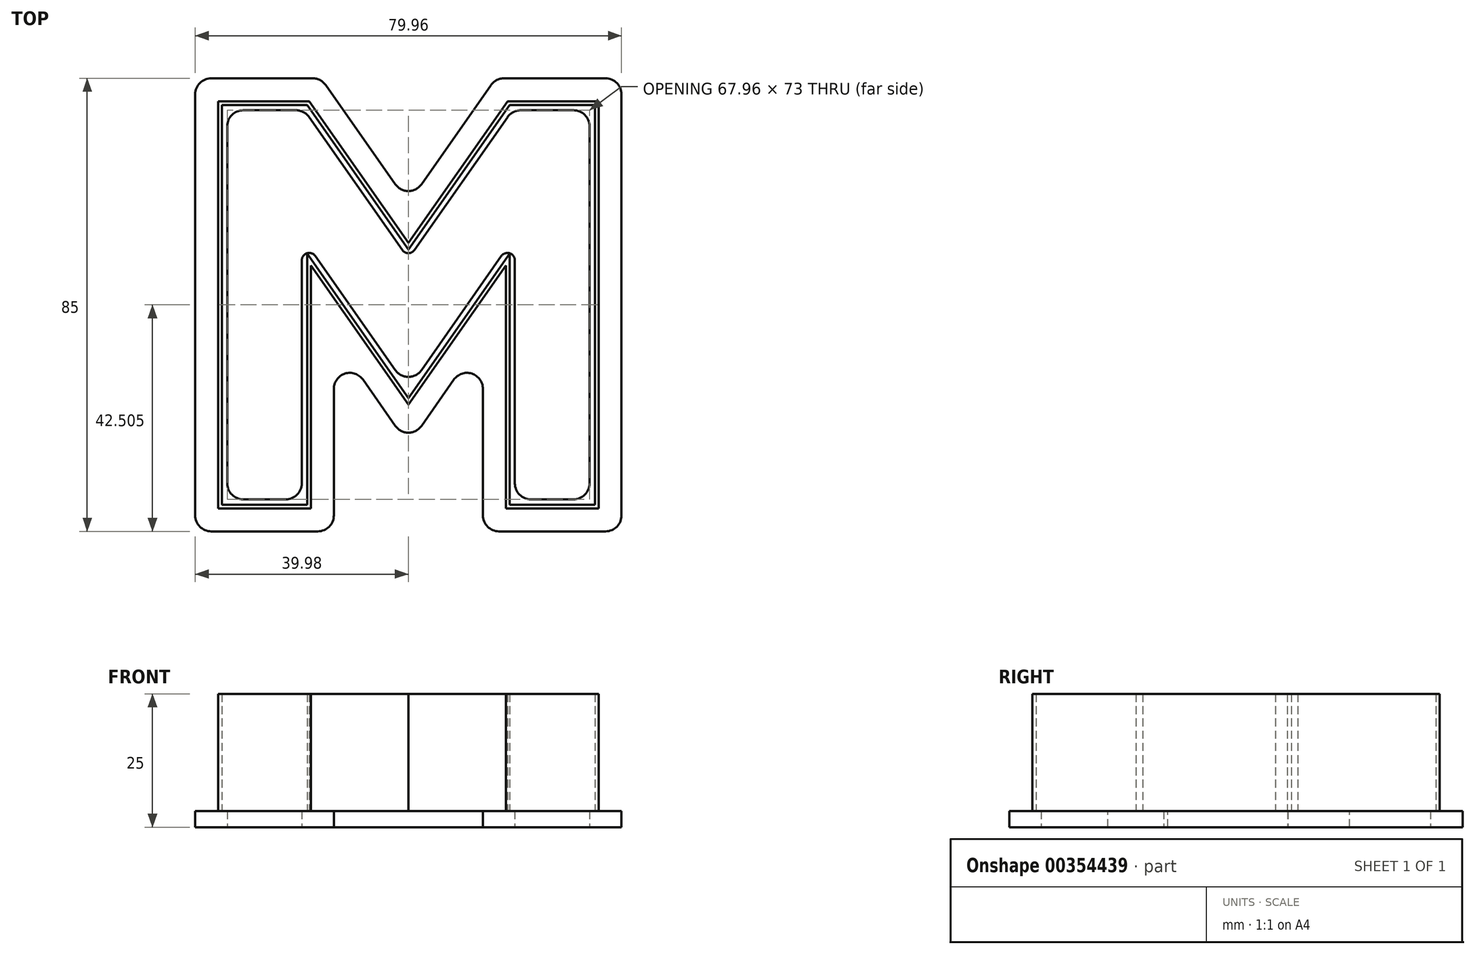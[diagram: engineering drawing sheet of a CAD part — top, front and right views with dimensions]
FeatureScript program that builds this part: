
annotation { "Feature Type Name" : "Feature", "Feature Type Description" : "" }
export const myFeature = defineFeature(function(context is Context, id is Id, definition is map)
    precondition{}
    {
        {
            var Q0;
            Q0=qCreatedBy(makeId("Top.planeOp"),FACE);
            var sketch = newSketch(context, id + "F0", { "sketchPlane" : qUnion([Q0])});
            skLineSegment(sketch, "E0", {"start": v(-34.98, -47.9) * mm, "end": v(-34.98, 27.1) * mm});
            skLineSegment(sketch, "E1", {"start": v(-34.98, 27.1) * mm, "end": v(-18.98, 27.1) * mm});
            skLineSegment(sketch, "E2", {"start": v(-18.98, 27.1) * mm, "end": v(0, 0) * mm});
            skLineSegment(sketch, "E3", {"start": v(0, 0) * mm, "end": v(18.98, 27.1) * mm});
            skLineSegment(sketch, "E4", {"start": v(18.98, 27.1) * mm, "end": v(34.98, 27.1) * mm});
            skLineSegment(sketch, "E5", {"start": v(34.98, 27.1) * mm, "end": v(34.98, -47.9) * mm});
            skLineSegment(sketch, "E6", {"start": v(34.98, -47.9) * mm, "end": v(18.98, -47.9) * mm});
            skLineSegment(sketch, "E7", {"start": v(18.98, -47.9) * mm, "end": v(18.98, -0.8) * mm});
            skLineSegment(sketch, "E8", {"start": v(18.98, -0.8) * mm, "end": v(0, -27.9) * mm});
            skLineSegment(sketch, "E9", {"start": v(-34.98, -47.9) * mm, "end": v(-18.98, -47.9) * mm});
            skLineSegment(sketch, "E10", {"start": v(-18.98, -47.9) * mm, "end": v(-18.98, -0.8) * mm});
            skLineSegment(sketch, "E11", {"start": v(-18.98, -0.8) * mm, "end": v(0, -27.9) * mm});
            skLineSegment(sketch, "E12", {"start": v(0, 0) * mm, "end": v(0, -47.9) * mm, "construction": true});
            skLineSegment(sketch, "E13", {"start": v(-18.98, -47.9) * mm, "end": v(0, -47.9) * mm, "construction": true});
            skLineSegment(sketch, "E14", {"start": v(0, -47.9) * mm, "end": v(18.98, -47.9) * mm, "construction": true});
            skLineSegment(sketch, "E15", {"start": v(-18.98, 27.1) * mm, "end": v(18.98, 27.1) * mm, "construction": true});
            skLineSegment(sketch, "E16.0", {"start": v(-33.98, -46.9) * mm, "end": v(-33.98, 26.1) * mm});
            skLineSegment(sketch, "E16.1", {"start": v(33.98, 26.1) * mm, "end": v(33.98, -46.9) * mm});
            skLineSegment(sketch, "E16.2", {"start": v(19.5, 26.1) * mm, "end": v(33.98, 26.1) * mm});
            skLineSegment(sketch, "E16.3", {"start": v(0, -1.74) * mm, "end": v(19.5, 26.1) * mm});
            skLineSegment(sketch, "E16.4", {"start": v(-19.5, 26.1) * mm, "end": v(0, -1.74) * mm});
            skLineSegment(sketch, "E16.5", {"start": v(33.98, -46.9) * mm, "end": v(19.98, -46.9) * mm});
            skLineSegment(sketch, "E16.6", {"start": v(-33.98, 26.1) * mm, "end": v(-19.5, 26.1) * mm});
            skLineSegment(sketch, "E16.7", {"start": v(19.98, -46.9) * mm, "end": v(19.98, 2.38) * mm});
            skLineSegment(sketch, "E16.8", {"start": v(19.98, 2.38) * mm, "end": v(0, -26.15) * mm});
            skLineSegment(sketch, "E16.9", {"start": v(-19.98, 2.38) * mm, "end": v(0, -26.15) * mm});
            skLineSegment(sketch, "E16.10", {"start": v(-19.98, -46.9) * mm, "end": v(-19.98, 2.38) * mm});
            skLineSegment(sketch, "E16.11", {"start": v(-33.98, -46.9) * mm, "end": v(-19.98, -46.9) * mm});
            skLineSegment(sketch, "E17.0", {"start": v(-39.98, -52.9) * mm, "end": v(-13.98, -52.9) * mm});
            skLineSegment(sketch, "E17.1", {"start": v(16.38, 32.1) * mm, "end": v(39.98, 32.1) * mm});
            skLineSegment(sketch, "E17.2", {"start": v(0, 8.72) * mm, "end": v(16.38, 32.1) * mm});
            skLineSegment(sketch, "E17.3", {"start": v(-16.38, 32.1) * mm, "end": v(0, 8.72) * mm});
            skLineSegment(sketch, "E17.4", {"start": v(-39.98, 32.1) * mm, "end": v(-16.38, 32.1) * mm});
            skLineSegment(sketch, "E17.5", {"start": v(39.98, 32.1) * mm, "end": v(39.98, -52.9) * mm});
            skLineSegment(sketch, "E17.6", {"start": v(-39.98, -52.9) * mm, "end": v(-39.98, 32.1) * mm});
            skLineSegment(sketch, "E17.7", {"start": v(39.98, -52.9) * mm, "end": v(13.98, -52.9) * mm});
            skLineSegment(sketch, "E17.8", {"start": v(13.98, -52.9) * mm, "end": v(13.98, -16.65) * mm});
            skLineSegment(sketch, "E17.9", {"start": v(13.98, -16.65) * mm, "end": v(0, -36.61) * mm});
            skLineSegment(sketch, "E17.10", {"start": v(-13.98, -16.65) * mm, "end": v(0, -36.61) * mm});
            skLineSegment(sketch, "E17.11", {"start": v(-13.98, -52.9) * mm, "end": v(-13.98, -16.65) * mm});
            skLineSegment(sketch, "E18.0", {"start": v(-35.68, -48.6) * mm, "end": v(-18.28, -48.6) * mm});
            skLineSegment(sketch, "E18.1", {"start": v(18.61, 27.8) * mm, "end": v(35.68, 27.8) * mm});
            skLineSegment(sketch, "E18.2", {"start": v(0, 1.22) * mm, "end": v(18.61, 27.8) * mm});
            skLineSegment(sketch, "E18.3", {"start": v(-18.61, 27.8) * mm, "end": v(0, 1.22) * mm});
            skLineSegment(sketch, "E18.4", {"start": v(-35.68, 27.8) * mm, "end": v(-18.61, 27.8) * mm});
            skLineSegment(sketch, "E18.5", {"start": v(35.68, 27.8) * mm, "end": v(35.68, -48.6) * mm});
            skLineSegment(sketch, "E18.6", {"start": v(-35.68, -48.6) * mm, "end": v(-35.68, 27.8) * mm});
            skLineSegment(sketch, "E18.7", {"start": v(35.68, -48.6) * mm, "end": v(18.28, -48.6) * mm});
            skLineSegment(sketch, "E18.8", {"start": v(18.28, -48.6) * mm, "end": v(18.28, -3.01) * mm});
            skLineSegment(sketch, "E18.9", {"start": v(18.28, -3.01) * mm, "end": v(0, -29.12) * mm});
            skLineSegment(sketch, "E18.10", {"start": v(-18.28, -3.01) * mm, "end": v(0, -29.12) * mm});
            skLineSegment(sketch, "E18.11", {"start": v(-18.28, -48.6) * mm, "end": v(-18.28, -3.01) * mm});
            skSolve(sketch);
        }
        {
            var Q0;
            Q0=makeQuery(id+"F0.imprint","IMPRINT",FACE,{"disambiguationData":[TD([[makeQuery(id+"F0.imprint","IMPRINT",EDGE,{"derivedFrom":sQuery(id+"F0.wireOp",EDGE,"E17.0")}),1.0]])]});
            var Q1;
            Q1=makeQuery(id+"F0.imprint","IMPRINT",FACE,{"disambiguationData":[TD([[makeQuery(id+"F0.imprint","IMPRINT",EDGE,{"derivedFrom":sQuery(id+"F0.wireOp",EDGE,"E0")}),-1.0]])]});
            var Q2;
            Q2=makeQuery(id+"F0.imprint","IMPRINT",FACE,{"disambiguationData":[TD([[makeQuery(id+"F0.imprint","IMPRINT",EDGE,{"derivedFrom":sQuery(id+"F0.wireOp",EDGE,"E0")}),1.0]])]});
            extrude(context, id + "F1", {"entities" : qUnion([Q0, Q1, Q2]), "depth" : 3 * mm});
        }
        {
            var Q0;
            Q0=makeQuery(id+"F0.imprint","IMPRINT",FACE,{"disambiguationData":[TD([[makeQuery(id+"F0.imprint","IMPRINT",EDGE,{"derivedFrom":sQuery(id+"F0.wireOp",EDGE,"E0")}),1.0]])]});
            extrude(context, id + "F2", {"entities" : qUnion([Q0]), "operationType" : NewBodyOperationType.ADD, "depth" : 25 * mm});
        }
        {
            var Q0;
            Q0=makeQuery(id+"F1.opExtrude","SWEPT_EDGE",EDGE,{"disambiguationData":[OSD([sQuery(id+"F0.wireOp",EDGE,"E16.2"),sQuery(id+"F0.wireOp",EDGE,"E16.3")])]});
            var Q1;
            Q1=makeQuery(id+"F1.opExtrude","SWEPT_EDGE",EDGE,{"disambiguationData":[OSD([sQuery(id+"F0.wireOp",EDGE,"E16.1"),sQuery(id+"F0.wireOp",EDGE,"E16.2")])]});
            var Q2;
            Q2=makeQuery(id+"F1.opExtrude","SWEPT_EDGE",EDGE,{"disambiguationData":[OSD([sQuery(id+"F0.wireOp",EDGE,"E16.0"),sQuery(id+"F0.wireOp",EDGE,"E16.11")])]});
            var Q3;
            Q3=makeQuery(id+"F1.opExtrude","SWEPT_EDGE",EDGE,{"disambiguationData":[OSD([sQuery(id+"F0.wireOp",EDGE,"E16.10"),sQuery(id+"F0.wireOp",EDGE,"E16.11")])]});
            var Q4;
            Q4=makeQuery(id+"F1.opExtrude","SWEPT_EDGE",EDGE,{"disambiguationData":[OSD([sQuery(id+"F0.wireOp",EDGE,"E17.0"),sQuery(id+"F0.wireOp",EDGE,"E17.6")])]});
            var Q5;
            Q5=makeQuery(id+"F1.opExtrude","SWEPT_EDGE",EDGE,{"disambiguationData":[OSD([sQuery(id+"F0.wireOp",EDGE,"E17.0"),sQuery(id+"F0.wireOp",EDGE,"E17.11")])]});
            var Q6;
            Q6=makeQuery(id+"F1.opExtrude","SWEPT_EDGE",EDGE,{"disambiguationData":[OSD([sQuery(id+"F0.wireOp",EDGE,"E17.7"),sQuery(id+"F0.wireOp",EDGE,"E17.8")])]});
            var Q7;
            Q7=makeQuery(id+"F1.opExtrude","SWEPT_EDGE",EDGE,{"disambiguationData":[OSD([sQuery(id+"F0.wireOp",EDGE,"E17.5"),sQuery(id+"F0.wireOp",EDGE,"E17.7")])]});
            var Q8;
            Q8=makeQuery(id+"F1.opExtrude","SWEPT_EDGE",EDGE,{"disambiguationData":[OSD([sQuery(id+"F0.wireOp",EDGE,"E17.1"),sQuery(id+"F0.wireOp",EDGE,"E17.5")])]});
            var Q9;
            Q9=makeQuery(id+"F1.opExtrude","SWEPT_EDGE",EDGE,{"disambiguationData":[OSD([sQuery(id+"F0.wireOp",EDGE,"E17.1"),sQuery(id+"F0.wireOp",EDGE,"E17.2")])]});
            var Q10;
            Q10=makeQuery(id+"F1.opExtrude","SWEPT_EDGE",EDGE,{"disambiguationData":[OSD([sQuery(id+"F0.wireOp",EDGE,"E17.3"),sQuery(id+"F0.wireOp",EDGE,"E17.4")])]});
            var Q11;
            Q11=makeQuery(id+"F1.opExtrude","SWEPT_EDGE",EDGE,{"disambiguationData":[OSD([sQuery(id+"F0.wireOp",EDGE,"E17.2"),sQuery(id+"F0.wireOp",EDGE,"E17.3")])]});
            var Q12;
            Q12=makeQuery(id+"F1.opExtrude","SWEPT_EDGE",EDGE,{"disambiguationData":[OSD([sQuery(id+"F0.wireOp",EDGE,"E17.4"),sQuery(id+"F0.wireOp",EDGE,"E17.6")])]});
            var Q13;
            Q13=makeQuery(id+"F1.opExtrude","SWEPT_EDGE",EDGE,{"disambiguationData":[OSD([sQuery(id+"F0.wireOp",EDGE,"E17.9"),sQuery(id+"F0.wireOp",EDGE,"E17.10")])]});
            var Q14;
            Q14=makeQuery(id+"F1.opExtrude","SWEPT_EDGE",EDGE,{"disambiguationData":[OSD([sQuery(id+"F0.wireOp",EDGE,"E17.10"),sQuery(id+"F0.wireOp",EDGE,"E17.11")])]});
            var Q15;
            Q15=makeQuery(id+"F1.opExtrude","SWEPT_EDGE",EDGE,{"disambiguationData":[OSD([sQuery(id+"F0.wireOp",EDGE,"E17.8"),sQuery(id+"F0.wireOp",EDGE,"E17.9")])]});
            var Q16;
            Q16=makeQuery(id+"F1.opExtrude","SWEPT_EDGE",EDGE,{"disambiguationData":[OSD([sQuery(id+"F0.wireOp",EDGE,"E16.8"),sQuery(id+"F0.wireOp",EDGE,"E16.9")])]});
            var Q17;
            Q17=makeQuery(id+"F1.opExtrude","SWEPT_EDGE",EDGE,{"disambiguationData":[OSD([sQuery(id+"F0.wireOp",EDGE,"E16.4"),sQuery(id+"F0.wireOp",EDGE,"E16.6")])]});
            var Q18;
            Q18=makeQuery(id+"F1.opExtrude","SWEPT_EDGE",EDGE,{"disambiguationData":[OSD([sQuery(id+"F0.wireOp",EDGE,"E16.0"),sQuery(id+"F0.wireOp",EDGE,"E16.6")])]});
            var Q19;
            Q19=makeQuery(id+"F1.opExtrude","SWEPT_EDGE",EDGE,{"disambiguationData":[OSD([sQuery(id+"F0.wireOp",EDGE,"E16.1"),sQuery(id+"F0.wireOp",EDGE,"E16.5")])]});
            var Q20;
            Q20=makeQuery(id+"F1.opExtrude","SWEPT_EDGE",EDGE,{"disambiguationData":[OSD([sQuery(id+"F0.wireOp",EDGE,"E16.5"),sQuery(id+"F0.wireOp",EDGE,"E16.7")])]});
            fillet(context, id + "F3", {"entities" : qUnion([Q0, Q1, Q2, Q3, Q4, Q5, Q6, Q7, Q8, Q9, Q10, Q11, Q12, Q13, Q14, Q15, Q16, Q17, Q18, Q19, Q20]), "radius" : 3 * mm, "tangentPropagation" : true, "allowEdgeOverflow" : false});
        }
        {
            var Q0;
            Q0=makeQuery(id+"F1.opExtrude","SWEPT_EDGE",EDGE,{"disambiguationData":[OSD([sQuery(id+"F0.wireOp",EDGE,"E16.9"),sQuery(id+"F0.wireOp",EDGE,"E16.10")])]});
            var Q1;
            Q1=makeQuery(id+"F1.opExtrude","SWEPT_EDGE",EDGE,{"disambiguationData":[OSD([sQuery(id+"F0.wireOp",EDGE,"E16.7"),sQuery(id+"F0.wireOp",EDGE,"E16.8")])]});
            var Q2;
            Q2=makeQuery(id+"F1.opExtrude","SWEPT_EDGE",EDGE,{"disambiguationData":[OSD([sQuery(id+"F0.wireOp",EDGE,"E16.3"),sQuery(id+"F0.wireOp",EDGE,"E16.4")])]});
            fillet(context, id + "F4", {"entities" : qUnion([Q0, Q1, Q2]), "radius" : 1.4 * mm, "tangentPropagation" : true, "allowEdgeOverflow" : false});
        }
    });
